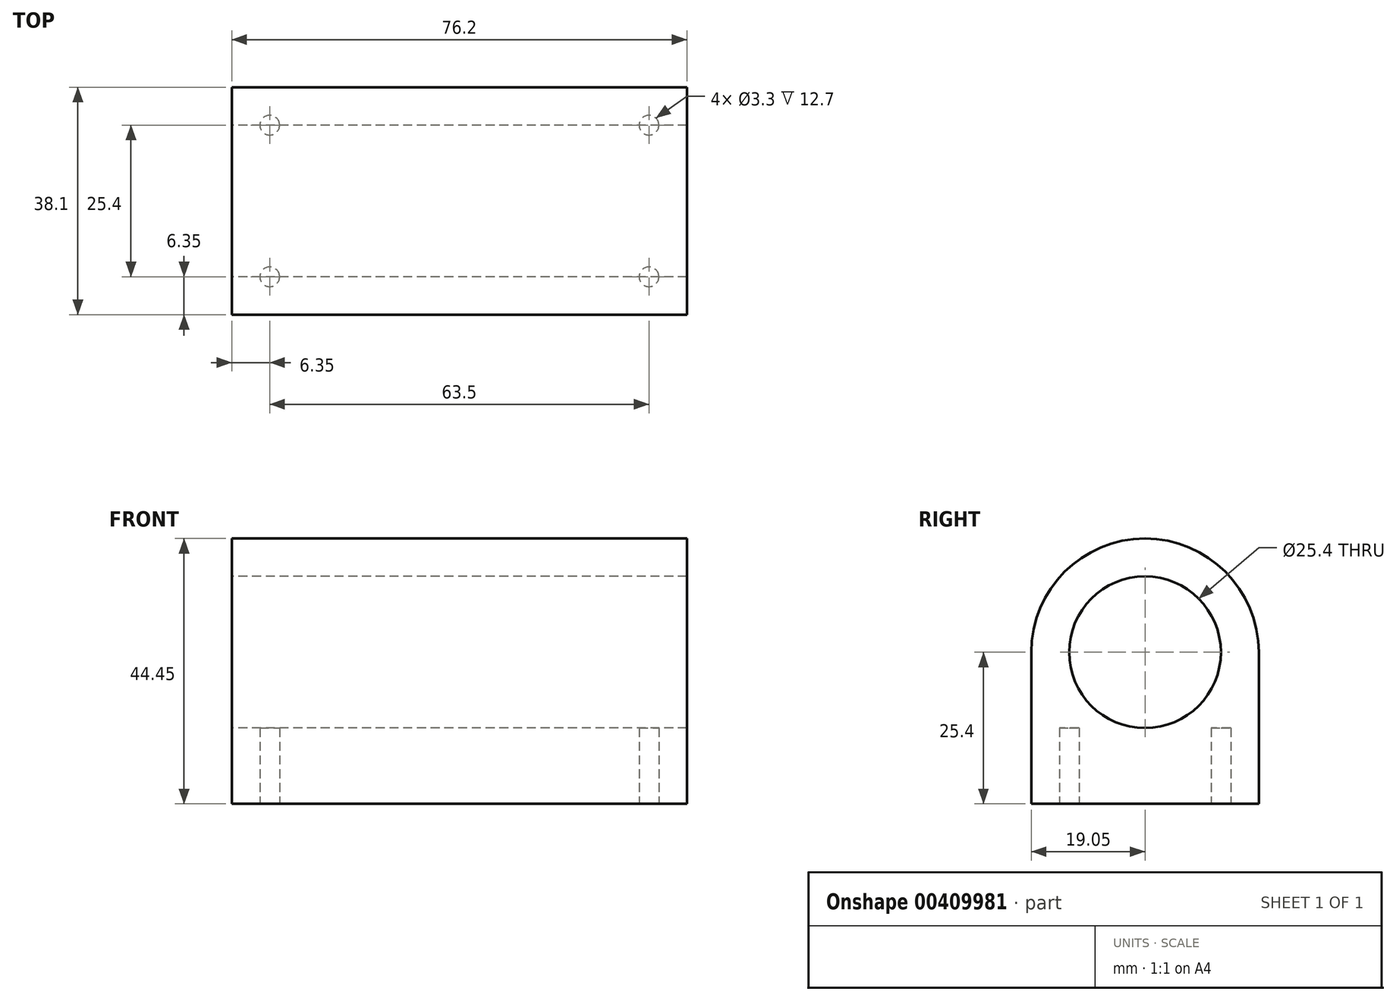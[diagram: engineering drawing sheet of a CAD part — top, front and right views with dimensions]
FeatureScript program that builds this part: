
annotation { "Feature Type Name" : "Feature", "Feature Type Description" : "" }
export const myFeature = defineFeature(function(context is Context, id is Id, definition is map)
    precondition{}
    {
        {
            var Q0;
            Q0=qCreatedBy(makeId("Right.planeOp"),FACE);
            var sketch = newSketch(context, id + "F0", { "sketchPlane" : qUnion([Q0])});
            skLineSegment(sketch, "E0", {"start": v(0, 16.2) * mm, "end": v(0, -26.8) * mm, "construction": true});
            skLineSegment(sketch, "E1", {"start": v(-25.3, 0) * mm, "end": v(23.3, 0) * mm, "construction": true});
            skCircle(sketch, "E2", {"center": v(0, 0) * mm, "radius": 12.7 * mm});
            skArc(sketch, "E3", {"start": v(19.05, 0) * mm, "mid": v(0, 19.05) * mm, "end": v(-19.05, 0) * mm});
            skPoint(sketch, "E4.MirrorCS.start.orphan", {"position": v(19.05, 0) * mm});
            skLineSegment(sketch, "E5", {"start": v(-19.05, 0) * mm, "end": v(-19.05, -25.4) * mm});
            skLineSegment(sketch, "E6", {"start": v(-19.05, -25.4) * mm, "end": v(0, -25.4) * mm});
            skLineSegment(sketch, "E7.MirrorCS", {"start": v(19.05, -25.4) * mm, "end": v(0, -25.4) * mm});
            skLineSegment(sketch, "E8.MirrorCS", {"start": v(19.05, 0) * mm, "end": v(19.05, -25.4) * mm});
            skSolve(sketch);
        }
        {
            var Q0;
            Q0 = qSketchRegion(id + "F0", true);
            extrude(context, id + "F1", {"entities" : qUnion([Q0]), "endBound" : BoundingType.SYMMETRIC, "depth" : 76.2 * mm});
        }
        {
            var Q0;
            Q0=makeQuery(id+"F1.opExtrude","SWEPT_FACE",FACE,{"disambiguationData":[OSD([sQuery(id+"F0.wireOp",EDGE,"E6"),sQuery(id+"F0.wireOp",EDGE,"E7.MirrorCS")])]});
            var sketch = newSketch(context, id + "F2", { "sketchPlane" : qUnion([Q0])});
            skLineSegment(sketch, "E9", {"start": v(0, -25.25) * mm, "end": v(0, 22.23) * mm, "construction": true});
            skLineSegment(sketch, "E10", {"start": v(39.42, 0) * mm, "end": v(-45.61, 0) * mm, "construction": true});
            skLineSegment(sketch, "E11", {"start": v(31.75, -23.16) * mm, "end": v(31.75, 27.96) * mm, "construction": true});
            skCircle(sketch, "E12", {"center": v(31.75, -12.7) * mm, "radius": 1.65 * mm});
            skCircle(sketch, "E13", {"center": v(31.75, 12.7) * mm, "radius": 1.65 * mm});
            skCircle(sketch, "E14.MirrorC", {"center": v(-31.75, -12.7) * mm, "radius": 1.65 * mm});
            skLineSegment(sketch, "E15.MirrorCS", {"start": v(-31.75, -23.16) * mm, "end": v(-31.75, 27.96) * mm, "construction": true});
            skCircle(sketch, "E16.MirrorC", {"center": v(-31.75, 12.7) * mm, "radius": 1.65 * mm});
            skSolve(sketch);
        }
        {
            var Q0;
            Q0 = qSketchRegion(id + "F2", true);
            extrude(context, id + "F3", {"entities" : qUnion([Q0]), "operationType" : NewBodyOperationType.REMOVE, "oppositeDirection" : true, "depth" : 12.7 * mm});
        }
    });
